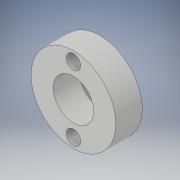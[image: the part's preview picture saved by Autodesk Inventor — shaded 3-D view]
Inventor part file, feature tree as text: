
AUTODESK INVENTOR PART (.ipt)
format: ipt  version: 2019 (Build 230136000, 136)  size: 158,720 bytes
history: native  units: in
note: dims shown in document units (in); Inventor stores cm internally (conversion verified against a paired STEP export)
features: extrude x3, sketch x3, plane x1
ambient origin geometry x8: Origin, YZ Plane, XZ Plane, XY Plane, X Axis, Y Axis, Z Axis, Center Point
bodies: Solid1 (feature_tree)
feature tree (7):
  plane  "Work Plane2"
  extrude  "Extrusion2"  Depth=0.136in
  extrude  "Extrusion4"  Depth=0.6185in
  extrude  "Extrusion5"  Depth=0.063in
  sketch  "Sketch3"  dims[d9=0.8in d10=0.136in]
  sketch  "Sketch4"  dims[d11=0.136in d12=0.6185in]
  sketch  "Sketch5"  dims[d13=0.3093in d14=0.384in d16=0.0in d17=0.25in d18=0.0in d26=0.3093in d27=0.45in d28=0.063in d29=0.0in d30=0.0625in d31=0.0625in d32=0.125in d33=0.125in d34=0.063in d35=0.0in]
